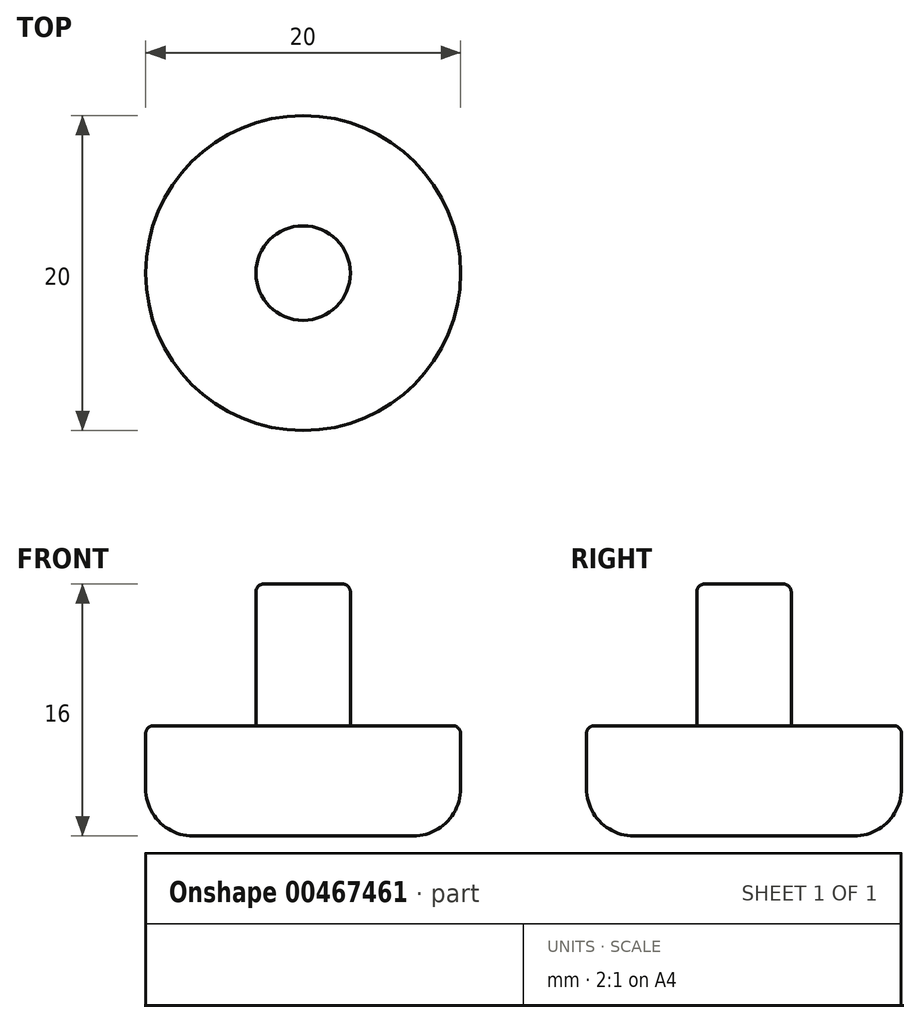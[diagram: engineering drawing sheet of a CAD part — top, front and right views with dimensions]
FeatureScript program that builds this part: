
annotation { "Feature Type Name" : "Feature", "Feature Type Description" : "" }
export const myFeature = defineFeature(function(context is Context, id is Id, definition is map)
    precondition{}
    {
        {
            var Q0;
            Q0=qCreatedBy(makeId("Top.planeOp"),FACE);
            var sketch = newSketch(context, id + "F0", { "sketchPlane" : qUnion([Q0])});
            skCircle(sketch, "E0", {"center": v(0, 0) * mm, "radius": 10 * mm});
            skSolve(sketch);
        }
        {
            var Q0;
            Q0 = qSketchRegion(id + "F0", true);
            extrude(context, id + "F1", {"entities" : qUnion([Q0]), "oppositeDirection" : true, "depth" : 7 * mm});
        }
        {
            var Q0;
            Q0=makeQuery(id+"F1.opExtrude","CAP_FACE",FACE,{"disambiguationData":[OSD([sQuery(id+"F0.wireOp",EDGE,"E0")])],"isStart":true});
            var sketch = newSketch(context, id + "F2", { "sketchPlane" : qUnion([Q0])});
            skCircle(sketch, "E1", {"center": v(0, 0) * mm, "radius": 3 * mm});
            skSolve(sketch);
        }
        {
            var Q0;
            Q0=makeQuery(id+"F2.imprint","IMPRINT",FACE,{"disambiguationData":[TD([[makeQuery(id+"F2.imprint","IMPRINT",EDGE,{"derivedFrom":sQuery(id+"F2.wireOp",EDGE,"E1")}),1.0]])]});
            extrude(context, id + "F3", {"entities" : qUnion([Q0]), "operationType" : NewBodyOperationType.ADD, "depth" : 9 * mm});
        }
        {
            var Q0;
            Q0=makeQuery(id+"F1.opExtrude","CAP_EDGE",EDGE,{"disambiguationData":[OSD([sQuery(id+"F0.wireOp",EDGE,"E0")])],"isStart":false});
            fillet(context, id + "F4", {"entities" : qUnion([Q0]), "radius" : 3 * mm, "tangentPropagation" : true, "allowEdgeOverflow" : false});
        }
        {
            var Q0;
            Q0=makeQuery(id+"F1.opExtrude","CAP_EDGE",EDGE,{"disambiguationData":[OSD([sQuery(id+"F0.wireOp",EDGE,"E0")])],"isStart":true});
            var Q1;
            Q1=makeQuery(id+"F3.opExtrude","CAP_EDGE",EDGE,{"disambiguationData":[OSD([sQuery(id+"F2.wireOp",EDGE,"E1")])],"isStart":false});
            var Q2;
            Q2=makeQuery(id+"F3.opExtrude","CAP_EDGE",EDGE,{"disambiguationData":[OSD([sQuery(id+"F2.wireOp",EDGE,"E1")])],"isStart":true});
            fillet(context, id + "F5", {"entities" : qUnion([Q0, Q1, Q2]), "radius" : .5 * mm, "tangentPropagation" : true, "allowEdgeOverflow" : false});
        }
    });
